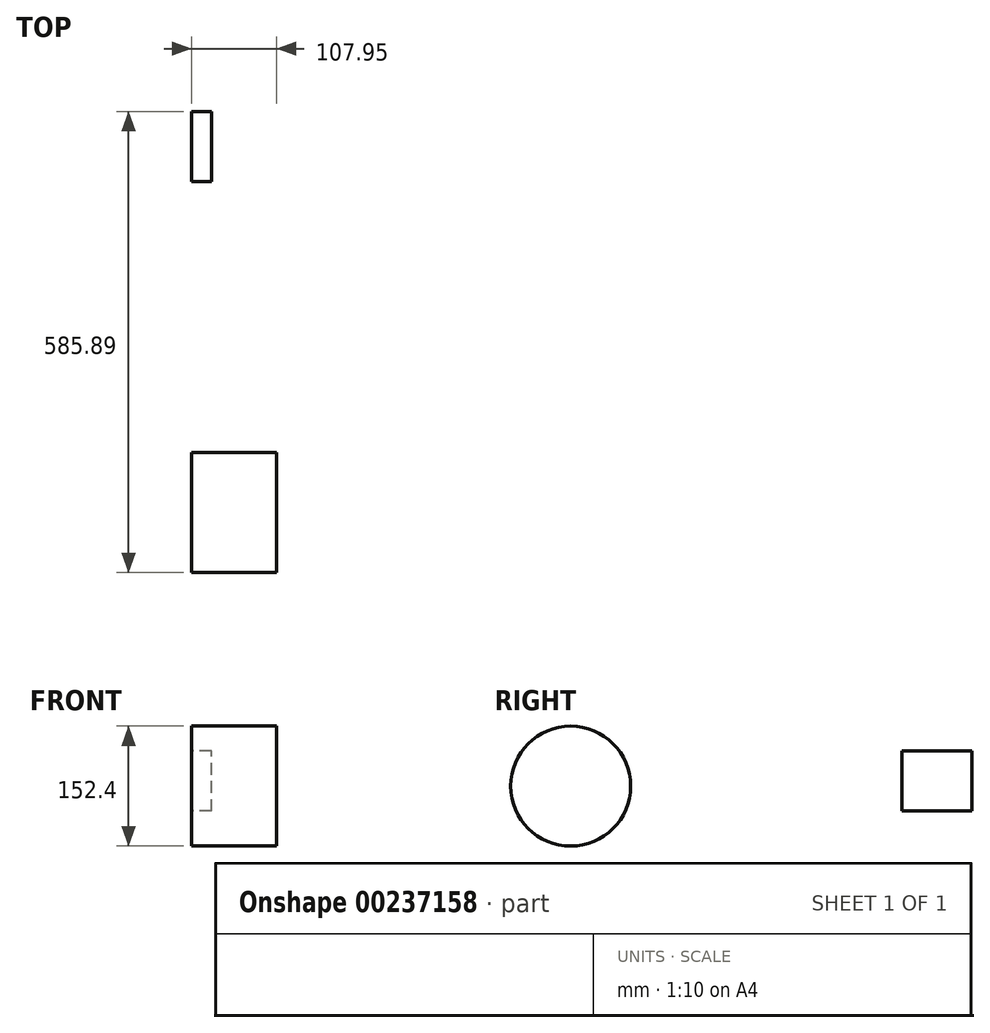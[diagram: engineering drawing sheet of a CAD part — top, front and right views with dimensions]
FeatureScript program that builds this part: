
annotation { "Feature Type Name" : "Feature", "Feature Type Description" : "" }
export const myFeature = defineFeature(function(context is Context, id is Id, definition is map)
    precondition{}
    {
        {
            var Q0;
            Q0=qCreatedBy(makeId("Right.planeOp"),FACE);
            var sketch = newSketch(context, id + "F0", { "sketchPlane" : qUnion([Q0])});
            skLineSegment(sketch, "E0.bottom", {"start": v(-51.04, -31.54) * mm, "end": v(37.86, -31.54) * mm});
            skLineSegment(sketch, "E0.top", {"start": v(-51.04, 44.66) * mm, "end": v(37.86, 44.66) * mm});
            skLineSegment(sketch, "E0.left", {"start": v(-51.04, -31.54) * mm, "end": v(-51.04, 44.66) * mm});
            skLineSegment(sketch, "E0.right", {"start": v(37.86, -31.54) * mm, "end": v(37.86, 44.66) * mm});
            skSolve(sketch);
        }
        {
            var Q0;
            Q0 = qSketchRegion(id + "F0", true);
            extrude(context, id + "F1", {"entities" : qUnion([Q0]), "depth" : 25.4 * mm});
        }
        {
            var Q0;
            Q0=qCreatedBy(makeId("Right.planeOp"),FACE);
            var sketch = newSketch(context, id + "F2", { "sketchPlane" : qUnion([Q0])});
            skCircle(sketch, "E1", {"center": v(-471.83, 0) * mm, "radius": 76.2 * mm});
            skLineSegment(sketch, "E2", {"start": v(-471.83, 0) * mm, "end": v(-471.83, 76.2) * mm});
            skSolve(sketch);
        }
        {
            var Q0;
            Q0 = qSketchRegion(id + "F2", true);
            extrude(context, id + "F3", {"entities" : qUnion([Q0]), "depth" : 107.95 * mm});
        }
    });
